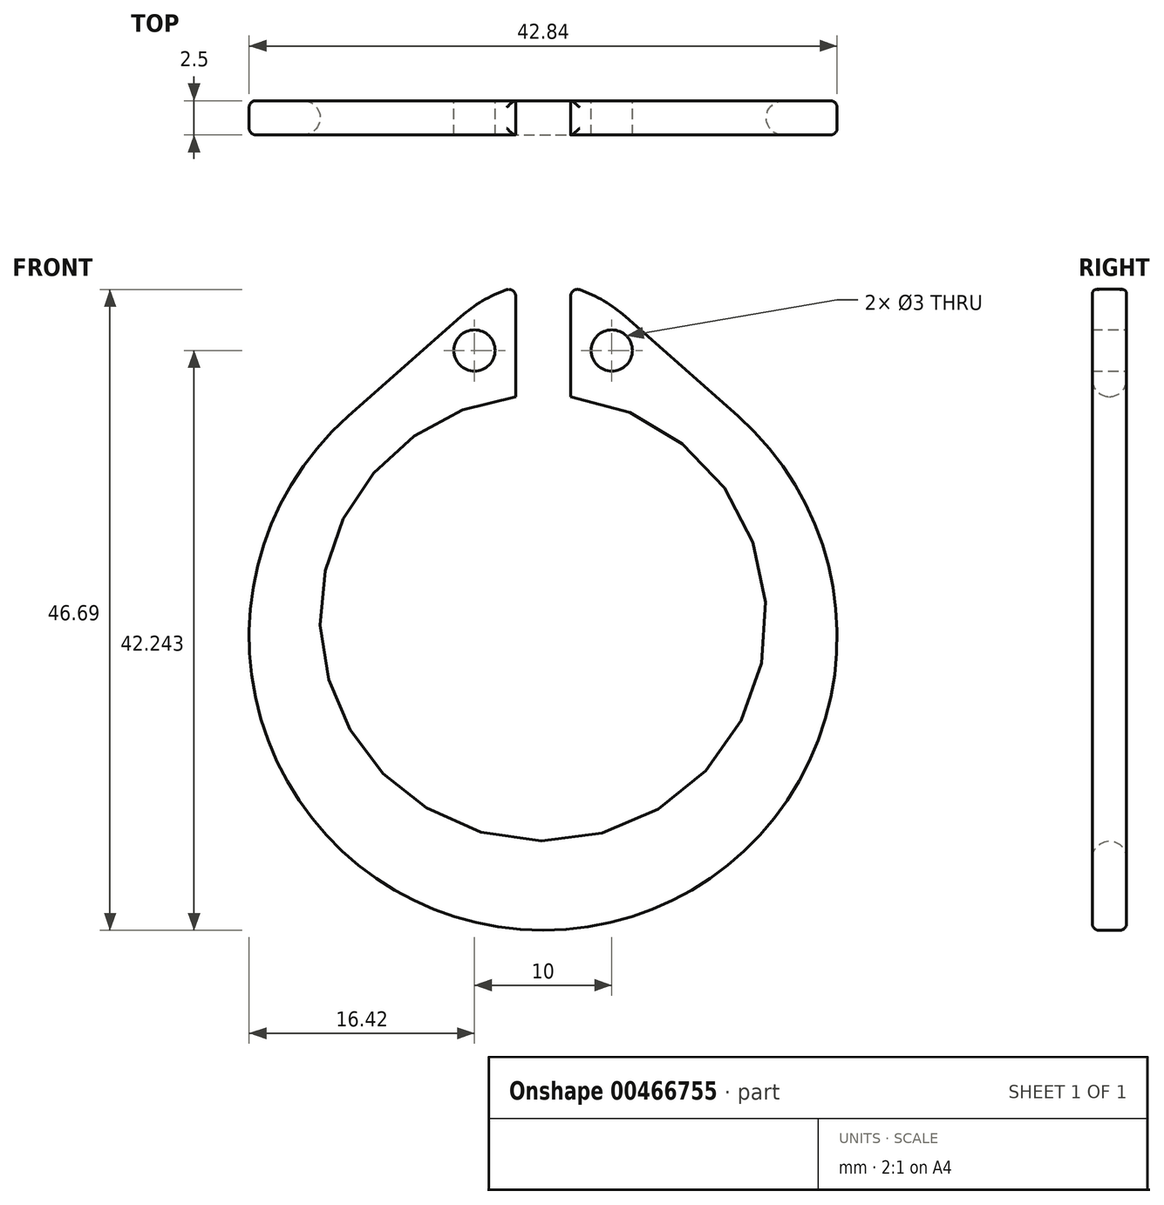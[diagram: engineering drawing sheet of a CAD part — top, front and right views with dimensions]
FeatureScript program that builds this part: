
annotation { "Feature Type Name" : "Feature", "Feature Type Description" : "" }
export const myFeature = defineFeature(function(context is Context, id is Id, definition is map)
    precondition{}
    {
        {
            var Q0;
            Q0=qCreatedBy(makeId("Front.planeOp"),FACE);
            var sketch = newSketch(context, id + "F0", { "sketchPlane" : qUnion([Q0])});
            skCircle(sketch, "E0", {"center": v(0, 0) * mm, "radius": 42.4 * mm, "construction": true});
            skArc(sketch, "E1", {"start": v(-2, 16.13) * mm, "mid": v(0, -16.25) * mm, "end": v(2, 16.13) * mm});
            skArc(sketch, "E2", {"start": v(-14.18, 14.72) * mm, "mid": v(-20.03, -8.92) * mm, "end": v(0, -22.75) * mm});
            skLineSegment(sketch, "E3", {"start": v(-2, 24.13) * mm, "end": v(-2, 16.13) * mm});
            skCircle(sketch, "E4", {"center": v(-5, 19.5) * mm, "radius": 1.5 * mm});
            skLineSegment(sketch, "E5", {"start": v(-6, 21.95) * mm, "end": v(-14.18, 14.72) * mm});
            skArc(sketch, "E6.trimOffspring", {"start": v(-2, 24.13) * mm, "mid": v(-4.12, 23.26) * mm, "end": v(-6, 21.95) * mm});
            skLineSegment(sketch, "E7", {"start": v(0, 28.3) * mm, "end": v(0, -26.78) * mm, "construction": true});
            skArc(sketch, "E8.MirrorCS", {"start": v(14.18, 14.72) * mm, "mid": v(20.03, -8.92) * mm, "end": v(0, -22.75) * mm});
            skLineSegment(sketch, "E9.MirrorCS", {"start": v(6, 21.95) * mm, "end": v(14.18, 14.72) * mm});
            skArc(sketch, "E10.MirrorCS", {"start": v(2, 24.13) * mm, "mid": v(4.12, 23.26) * mm, "end": v(6, 21.95) * mm});
            skLineSegment(sketch, "E11.MirrorCS", {"start": v(2, 24.13) * mm, "end": v(2, 16.13) * mm});
            skCircle(sketch, "E12.MirrorC", {"center": v(5, 19.5) * mm, "radius": 1.5 * mm});
            skSolve(sketch);
        }
        {
            var Q0;
            Q0 = qSketchRegion(id + "F0", true);
            extrude(context, id + "F1", {"entities" : qUnion([Q0]), "endBound" : BoundingType.SYMMETRIC, "depth" : 2.5 * mm});
        }
        {
            var Q0;
            Q0=makeQuery(id+"F1.opExtrude","CAP_EDGE",EDGE,{"disambiguationData":[OSD([sQuery(id+"F0.wireOp",EDGE,"E1")])],"isStart":false});
            var Q1;
            Q1=makeQuery(id+"F1.opExtrude","CAP_EDGE",EDGE,{"disambiguationData":[OSD([sQuery(id+"F0.wireOp",EDGE,"E1")])],"isStart":true});
            fillet(context, id + "F2", {"entities" : qUnion([Q0, Q1]), "radius" : 1.25 * mm, "tangentPropagation" : true, "allowEdgeOverflow" : false});
        }
        {
            var Q0;
            Q0=makeQuery(id+"F1.opExtrude","CAP_EDGE",EDGE,{"disambiguationData":[OSD([sQuery(id+"F0.wireOp",EDGE,"E2"),sQuery(id+"F0.wireOp",EDGE,"E8.MirrorCS")])],"isStart":false});
            var Q1;
            Q1=makeQuery(id+"F1.opExtrude","CAP_EDGE",EDGE,{"disambiguationData":[OSD([sQuery(id+"F0.wireOp",EDGE,"E2"),sQuery(id+"F0.wireOp",EDGE,"E8.MirrorCS")])],"isStart":true});
            var Q2;
            Q2=makeQuery(id+"F1.opExtrude","CAP_EDGE",EDGE,{"disambiguationData":[OSD([sQuery(id+"F0.wireOp",EDGE,"E9.MirrorCS")])],"isStart":true});
            var Q3;
            Q3=makeQuery(id+"F1.opExtrude","CAP_EDGE",EDGE,{"disambiguationData":[OSD([sQuery(id+"F0.wireOp",EDGE,"E9.MirrorCS")])],"isStart":false});
            var Q4;
            Q4=makeQuery(id+"F1.opExtrude","CAP_EDGE",EDGE,{"disambiguationData":[OSD([sQuery(id+"F0.wireOp",EDGE,"E10.MirrorCS")])],"isStart":false});
            var Q5;
            Q5=makeQuery(id+"F1.opExtrude","CAP_EDGE",EDGE,{"disambiguationData":[OSD([sQuery(id+"F0.wireOp",EDGE,"E10.MirrorCS")])],"isStart":true});
            var Q6;
            Q6=makeQuery(id+"F1.opExtrude","SWEPT_EDGE",EDGE,{"disambiguationData":[OSD([sQuery(id+"F0.wireOp",EDGE,"E10.MirrorCS"),sQuery(id+"F0.wireOp",EDGE,"E11.MirrorCS")])]});
            var Q7;
            Q7=makeQuery(id+"F1.opExtrude","CAP_EDGE",EDGE,{"disambiguationData":[OSD([sQuery(id+"F0.wireOp",EDGE,"E5")])],"isStart":false});
            var Q8;
            Q8=makeQuery(id+"F1.opExtrude","CAP_EDGE",EDGE,{"disambiguationData":[OSD([sQuery(id+"F0.wireOp",EDGE,"E5")])],"isStart":true});
            var Q9;
            Q9=makeQuery(id+"F1.opExtrude","CAP_EDGE",EDGE,{"disambiguationData":[OSD([sQuery(id+"F0.wireOp",EDGE,"E6.trimOffspring")])],"isStart":false});
            var Q10;
            Q10=makeQuery(id+"F1.opExtrude","CAP_EDGE",EDGE,{"disambiguationData":[OSD([sQuery(id+"F0.wireOp",EDGE,"E6.trimOffspring")])],"isStart":true});
            var Q11;
            Q11=makeQuery(id+"F1.opExtrude","SWEPT_EDGE",EDGE,{"disambiguationData":[OSD([sQuery(id+"F0.wireOp",EDGE,"E3"),sQuery(id+"F0.wireOp",EDGE,"E6.trimOffspring")])]});
            fillet(context, id + "F3", {"entities" : qUnion([Q0, Q1, Q2, Q3, Q4, Q5, Q6, Q7, Q8, Q9, Q10, Q11]), "radius" : 0.5 * mm, "tangentPropagation" : true, "allowEdgeOverflow" : false});
        }
    });
